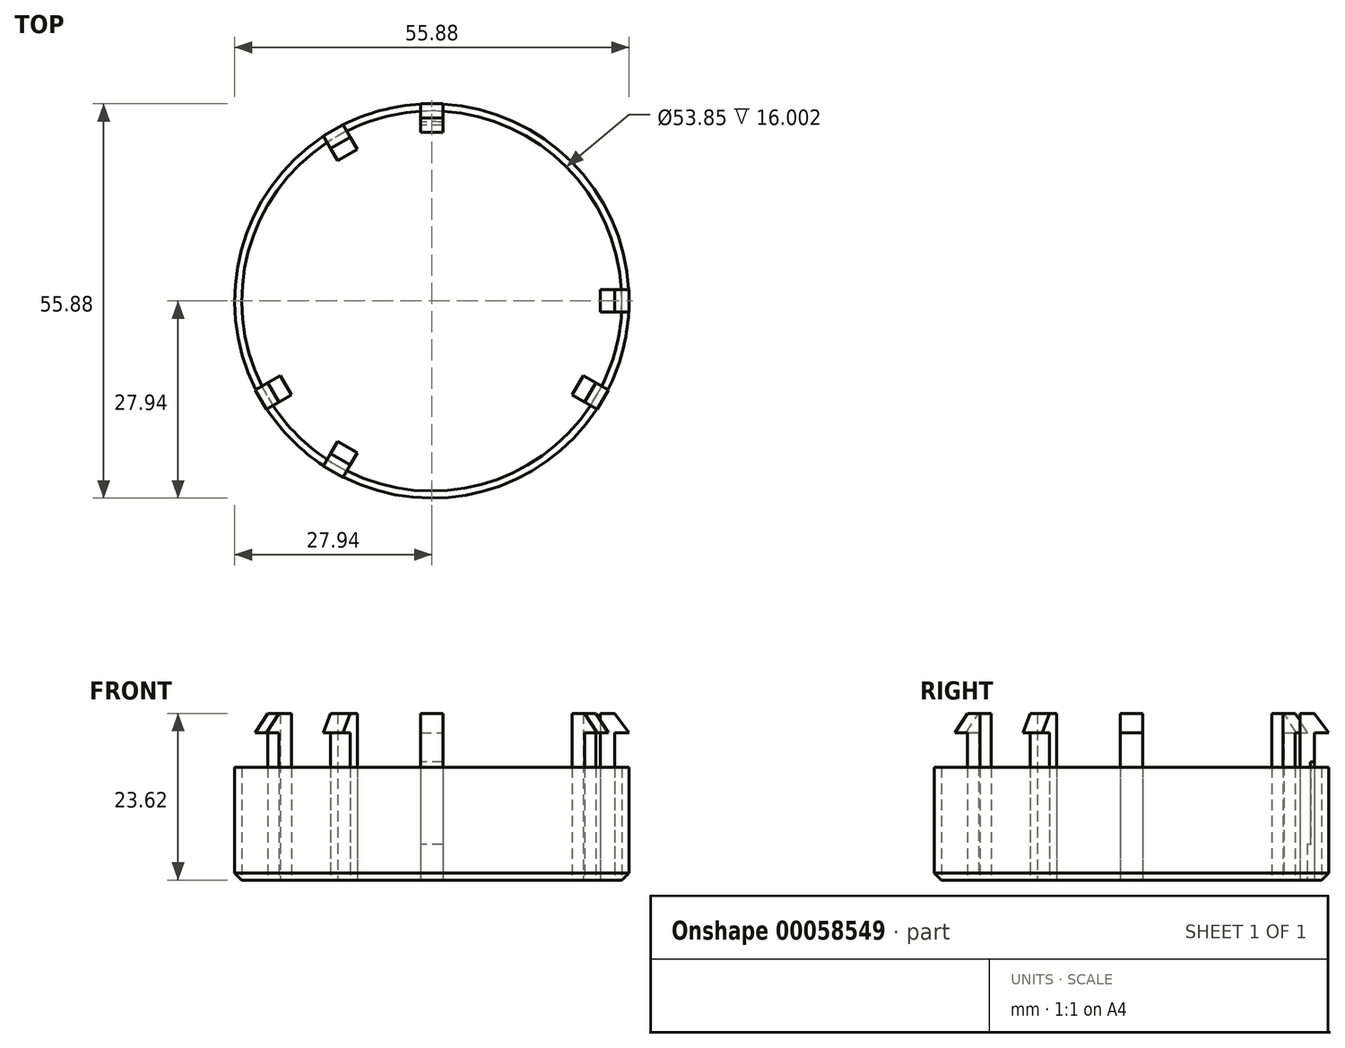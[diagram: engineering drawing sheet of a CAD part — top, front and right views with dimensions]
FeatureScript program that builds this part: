
annotation { "Feature Type Name" : "Feature", "Feature Type Description" : "" }
export const myFeature = defineFeature(function(context is Context, id is Id, definition is map)
    precondition{}
    {
        {
            var Q0;
            Q0=qCreatedBy(makeId("Top.planeOp"),FACE);
            var sketch = newSketch(context, id + "F0", { "sketchPlane" : qUnion([Q0])});
            skCircle(sketch, "E0", {"center": v(0, 0) * mm, "radius": 27.94 * mm});
            skCircle(sketch, "E1", {"center": v(0, 0) * mm, "radius": 25.4 * mm});
            skCircle(sketch, "E2", {"center": v(0, 0) * mm, "radius": 26.92 * mm});
            skCircle(sketch, "E3", {"center": v(0, 0) * mm, "radius": 22.23 * mm});
            skLineSegment(sketch, "E4.bottom", {"start": v(1.59, 25.9) * mm, "end": v(-1.59, 25.9) * mm});
            skLineSegment(sketch, "E4.top", {"start": v(1.59, 24.9) * mm, "end": v(-1.59, 24.9) * mm});
            skLineSegment(sketch, "E4.left", {"start": v(1.59, 25.9) * mm, "end": v(1.59, 24.9) * mm});
            skLineSegment(sketch, "E4.right", {"start": v(-1.59, 25.9) * mm, "end": v(-1.59, 24.9) * mm});
            skPoint(sketch, "E4.middle", {"position": v(0, 25.4) * mm});
            skLineSegment(sketch, "E5.bottom", {"start": v(-1.59, 24.9) * mm, "end": v(1.59, 24.9) * mm});
            skLineSegment(sketch, "E5.top", {"start": v(-1.59, 23.88) * mm, "end": v(1.59, 23.88) * mm});
            skLineSegment(sketch, "E5.left", {"start": v(-1.59, 24.9) * mm, "end": v(-1.59, 23.88) * mm});
            skLineSegment(sketch, "E5.right", {"start": v(1.59, 24.9) * mm, "end": v(1.59, 23.88) * mm});
            skSolve(sketch);
        }
        {
            var Q0;
            Q0=makeQuery(id+"F0.imprint","IMPRINT",FACE,{"disambiguationData":[TD([[makeQuery(id+"F0.imprint","IMPRINT",EDGE,{"derivedFrom":sQuery(id+"F0.wireOp",EDGE,"E1")}),-1.0]])]});
            extrude(context, id + "F1", {"entities" : qUnion([Q0]), "depth" : 16.76 * mm, "offsetDistance" : 25.4 * mm});
        }
        {
            var Q0;
            Q0=makeQuery(id+"F0.imprint","IMPRINT",FACE,{"disambiguationData":[TD([[makeQuery(id+"F0.imprint","IMPRINT",EDGE,{"derivedFrom":sQuery(id+"F0.wireOp",EDGE,"E0")}),1.0]])]});
            extrude(context, id + "F2", {"entities" : qUnion([Q0]), "operationType" : NewBodyOperationType.ADD, "depth" : 16 * mm, "offsetDistance" : 25.4 * mm});
        }
        {
            var Q0;
            Q0=makeQuery(id+"F0.imprint","IMPRINT",FACE,{"disambiguationData":[TD([[makeQuery(id+"F0.imprint","IMPRINT",EDGE,{"derivedFrom":sQuery(id+"F0.wireOp",EDGE,"E1")}),1.0]])]});
            extrude(context, id + "F3", {"entities" : qUnion([Q0]), "operationType" : NewBodyOperationType.ADD, "depth" : 5.08 * mm, "offsetDistance" : 25.4 * mm});
        }
        {
            var Q0;
            Q0=makeQuery(id+"F2.opExtrude","CAP_EDGE",EDGE,{"disambiguationData":[OSD([sQuery(id+"F0.wireOp",EDGE,"E0")])],"isStart":true});
            var Q1;
            Q1=makeQuery(id+"F3.opExtrude","CAP_EDGE",EDGE,{"disambiguationData":[OSD([sQuery(id+"F0.wireOp",EDGE,"E3")])],"isStart":true});
            chamfer(context, id + "F4", {"entities" : qUnion([Q0, Q1]), "width" : 1.02 * mm, "tangentPropagation" : true});
        }
        {
            var Q0;
            {var subQ5=sQuery(id+"F0.wireOp",EDGE,"E4.bottom");Q0=makeQuery(id+"F0.imprint","IMPRINT",FACE,{"disambiguationData":[TD([[makeQuery(id+"F0.imprint","IMPRINT",EDGE,{"derivedFrom":subQ5}),1.0]])]});}
            var Q1;
            {var subQ5=sQuery(id+"F0.wireOp",EDGE,"E4.top");Q1=makeQuery(id+"F0.imprint","IMPRINT",FACE,{"disambiguationData":[TD([[makeQuery(id+"F0.imprint","IMPRINT",EDGE,{"derivedFrom":subQ5}),-1.0]])]});}
            var Q2;
            Q2=makeQuery(id+"F0.imprint","IMPRINT",FACE,{"disambiguationData":[TD([[makeQuery(id+"F0.imprint","IMPRINT",EDGE,{"derivedFrom":sQuery(id+"F0.wireOp",EDGE,"E4.top")}),1.0]])]});
            extrude(context, id + "F5", {"entities" : qUnion([Q0, Q1, Q2]), "depth" : 23.62 * mm, "offsetDistance" : 25.4 * mm});
        }
        {
            var Q0;
            Q0=qCreatedBy(makeId("Right.planeOp"),FACE);
            var sketch = newSketch(context, id + "F6", { "sketchPlane" : qUnion([Q0])});
            skLineSegment(sketch, "E6", {"start": v(27.94, 20.9) * mm, "end": v(25.9, 23.62) * mm});
            skLineSegment(sketch, "E7", {"start": v(25.9, 23.62) * mm, "end": v(25.9, 23.62) * mm});
            skLineSegment(sketch, "E8", {"start": v(25.9, 20.9) * mm, "end": v(27.94, 20.9) * mm});
            skLineSegment(sketch, "E9", {"start": v(0, 0) * mm, "end": v(0, 21.46) * mm, "construction": true});
            skLineSegment(sketch, "E10", {"start": v(25.9, 23.62) * mm, "end": v(25.9, 20.9) * mm});
            skSolve(sketch);
        }
        {
            var Q0;
            Q0=makeQuery(id+"F6.imprint","IMPRINT",FACE,{"disambiguationData":[TD([[makeQuery(id+"F6.imprint","IMPRINT",EDGE,{"derivedFrom":sQuery(id+"F6.wireOp",EDGE,"E6")}),1.0]])]});
            extrude(context, id + "F7", {"entities" : qUnion([Q0]), "operationType" : NewBodyOperationType.ADD, "oppositeDirection" : true, "depth" : 3.17 * mm, "offsetDistance" : 25.4 * mm, "symmetric" : true});
        }
        {
            var Q0;
            Q0=makeQuery(id+"F5.opExtrude","SWEPT_BODY",BODY,{"disambiguationData":[OSD([sQuery(id+"F0.wireOp",EDGE,"E4.bottom"),sQuery(id+"F0.wireOp",EDGE,"E4.top"),sQuery(id+"F0.wireOp",EDGE,"E4.left"),sQuery(id+"F0.wireOp",EDGE,"E4.right")])]});
            var Q1;
            Q1=sQuery(id+"F6.wireOp",EDGE,"E9");
            circularPattern(context, id + "F8", {"entities" : qUnion([Q0]), "axis" : qUnion([Q1]), "angle" : 360 * degree, "instanceCount" : 3, "equalSpace" : true});
        }
        {
            var Q0;
            Q0=makeQuery(id+"F5.opExtrude","SWEPT_BODY",BODY,{"disambiguationData":[OSD([sQuery(id+"F0.wireOp",EDGE,"E4.bottom"),sQuery(id+"F0.wireOp",EDGE,"E4.top"),sQuery(id+"F0.wireOp",EDGE,"E4.left"),sQuery(id+"F0.wireOp",EDGE,"E4.right")])]});
            var Q1;
            Q1=sQuery(id+"F6.wireOp",EDGE,"E9");
            circularPattern(context, id + "F9", {"entities" : qUnion([Q0]), "axis" : qUnion([Q1]), "angle" : 30 * degree, "instanceCount" : 2});
        }
        {
            var Q0;
            Q0=makeQuery(id+"F9.opPattern","COPY",BODY,{"derivedFrom":makeQuery(id+"F5.opExtrude","SWEPT_BODY",BODY,{"disambiguationData":[OSD([sQuery(id+"F0.wireOp",EDGE,"E4.bottom"),sQuery(id+"F0.wireOp",EDGE,"E4.top"),sQuery(id+"F0.wireOp",EDGE,"E4.left"),sQuery(id+"F0.wireOp",EDGE,"E4.right")])]}),"instanceName":"1"});
            var Q1;
            Q1=sQuery(id+"F6.wireOp",EDGE,"E9");
            circularPattern(context, id + "F10", {"entities" : qUnion([Q0]), "axis" : qUnion([Q1]), "angle" : 360 * degree, "instanceCount" : 3, "equalSpace" : true});
        }
    });
